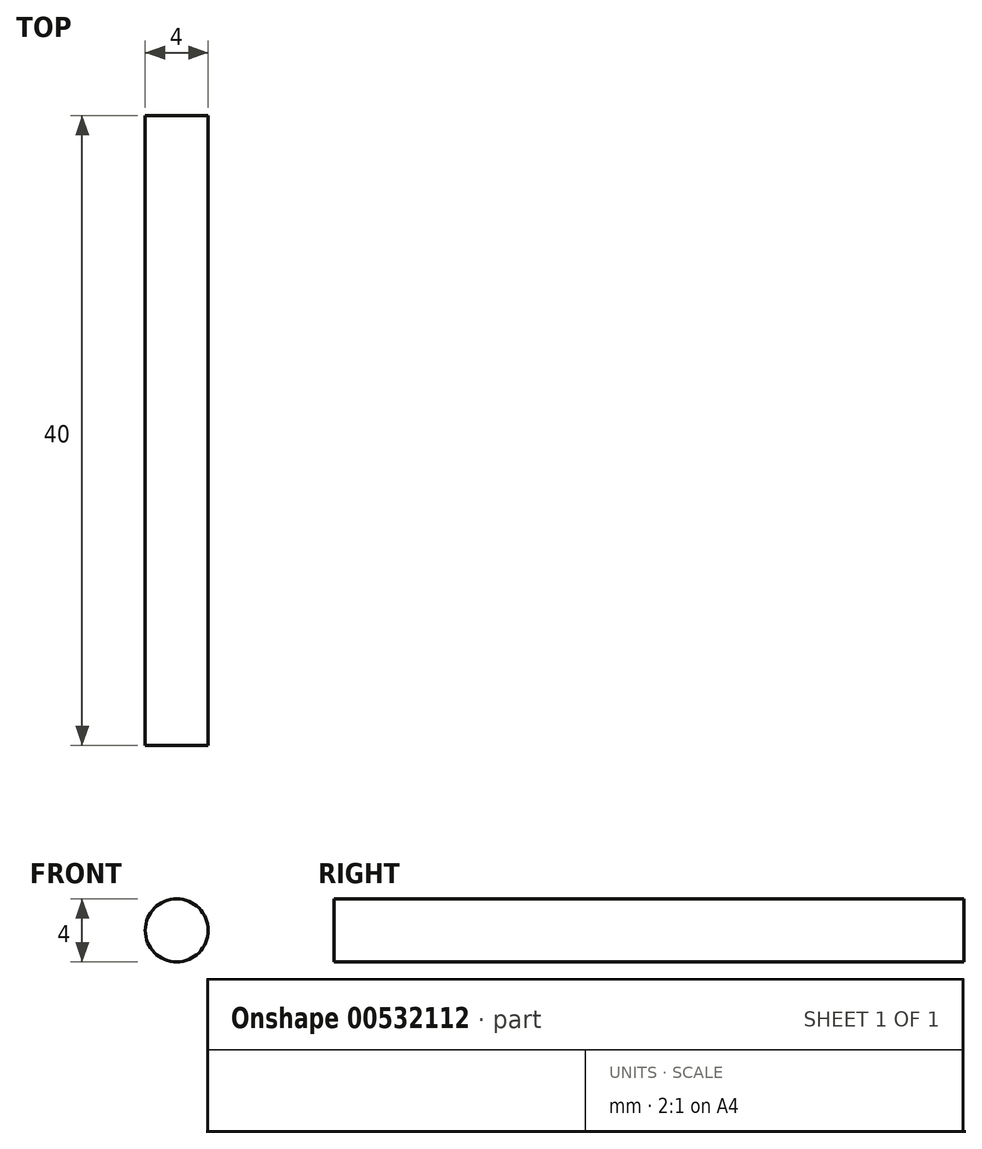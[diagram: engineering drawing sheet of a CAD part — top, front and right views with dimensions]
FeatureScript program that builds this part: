
annotation { "Feature Type Name" : "Feature", "Feature Type Description" : "" }
export const myFeature = defineFeature(function(context is Context, id is Id, definition is map)
    precondition{}
    {
        {
            var Q0;
            Q0=qCreatedBy(makeId("Front.planeOp"),FACE);
            var sketch = newSketch(context, id + "F0", { "sketchPlane" : qUnion([Q0])});
            skCircle(sketch, "E0", {"center": v(0, 0) * mm, "radius": 2 * mm});
            skSolve(sketch);
        }
        {
            var Q0;
            Q0=qSketchRegion(id+"F0",true);
            extrude(context, id + "F1", {"entities" : qUnion([Q0]), "depth" : 40 * mm, "offsetDistance" : 25.4 * mm});
        }
    });
